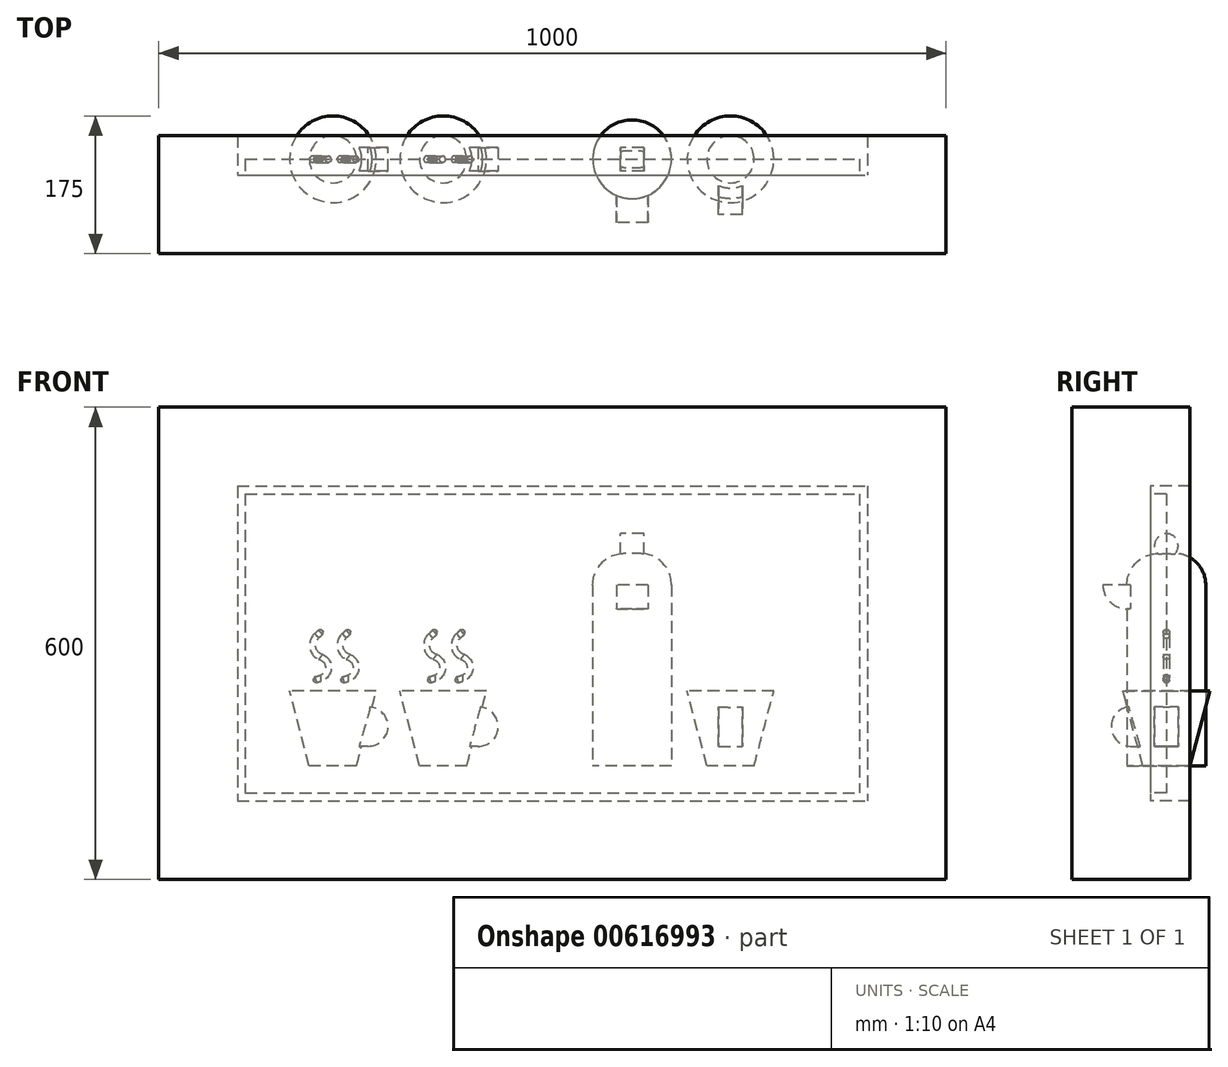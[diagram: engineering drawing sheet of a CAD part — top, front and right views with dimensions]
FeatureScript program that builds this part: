
annotation { "Feature Type Name" : "Feature", "Feature Type Description" : "" }
export const myFeature = defineFeature(function(context is Context, id is Id, definition is map)
    precondition{}
    {
        {
            var Q0;
            Q0=qCreatedBy(makeId("Top.planeOp"),FACE);
            cPlane(context, id + "F0", {"entities" : qUnion([Q0]), "cplaneType" : CPlaneType.OFFSET, "offset" : 95 * mm, "width" : 150 * mm, "height" : 150 * mm});
        }
        {
            var Q0;
            Q0=qCreatedBy(makeId("Top.planeOp"),FACE);
            var sketch = newSketch(context, id + "F1", { "sketchPlane" : qUnion([Q0])});
            skCircle(sketch, "E0", {"center": v(80, 0) * mm, "radius": 50 * mm});
            skSolve(sketch);
        }
        {
            var Q0;
            Q0=qSketchRegion(id+"F1",true);
            var Q1;
            Q1=qSketchRegion(id+"F3",true);
            extrude(context, id + "F2", {"entities" : qUnion([Q0, Q1]), "depth" : 230 * mm, "offsetDistance" : 25 * mm});
        }
        {
            var Q0;
            Q0=qCreatedBy(makeId("Top.planeOp"),FACE);
            var sketch = newSketch(context, id + "F3", { "sketchPlane" : qUnion([Q0])});
            skCircle(sketch, "E1", {"center": v(205, 0) * mm, "radius": 30 * mm});
            skSolve(sketch);
        }
        {
            var Q0;
            Q0=qCreatedBy(id+"F0.planeOp",FACE);
            var sketch = newSketch(context, id + "F4", { "sketchPlane" : qUnion([Q0])});
            skCircle(sketch, "E2", {"center": v(205, 0) * mm, "radius": 55 * mm});
            skSolve(sketch);
        }
        {
            var Q0;
            Q0=qCreatedBy(makeId("Top.planeOp"),FACE);
            cPlane(context, id + "F5", {"entities" : qUnion([Q0]), "cplaneType" : CPlaneType.OFFSET, "offset" : 230 * mm, "width" : 150 * mm, "height" : 150 * mm});
        }
        {
            var Q0;
            Q0=qCreatedBy(id+"F5.planeOp",FACE);
            var sketch = newSketch(context, id + "F6", { "sketchPlane" : qUnion([Q0])});
            skCircle(sketch, "E3", {"center": v(80, 0) * mm, "radius": 50 * mm});
            skSolve(sketch);
        }
        {
            var Q0;
            Q0 = qSketchRegion(id + "F6", true);
            extrude(context, id + "F7", {"entities" : qUnion([Q0]), "operationType" : NewBodyOperationType.ADD, "depth" : 40 * mm, "offsetDistance" : 25 * mm});
        }
        {
            var Q0;
            Q0=makeQuery(id+"F7.opExtrude","CAP_EDGE",EDGE,{"disambiguationData":[OSD([sQuery(id+"F6.wireOp",EDGE,"E3")])],"isStart":false});
            fillet(context, id + "F8", {"entities" : qUnion([Q0]), "radius" : 40 * mm, "tangentPropagation" : true, "allowEdgeOverflow" : false});
        }
        {
            var Q0;
            Q0=qSketchRegion(id+"F3",true);
            var Q1;
            Q1=qSketchRegion(id+"F4",true);
            loft(context, id + "F9", {"sheetProfilesArray" : [{ "sheetProfileEntities" : qUnion([Q0]) }, { "sheetProfileEntities" : qUnion([Q1]) }]});
        }
        {
            var Q0;
            Q0=qCreatedBy(makeId("Top.planeOp"),FACE);
            var sketch = newSketch(context, id + "F10", { "sketchPlane" : qUnion([Q0])});
            skCircle(sketch, "E4", {"center": v(-160, 0) * mm, "radius": 30 * mm});
            skSolve(sketch);
        }
        {
            var Q0;
            Q0=qCreatedBy(id+"F0.planeOp",FACE);
            var sketch = newSketch(context, id + "F11", { "sketchPlane" : qUnion([Q0])});
            skCircle(sketch, "E5", {"center": v(-160, 0) * mm, "radius": 55 * mm});
            skSolve(sketch);
        }
        {
            var Q0;
            Q0=qSketchRegion(id+"F10",true);
            var Q1;
            Q1=qSketchRegion(id+"F11",true);
            loft(context, id + "F12", {"sheetProfilesArray" : [{ "sheetProfileEntities" : qUnion([Q0]) }, { "sheetProfileEntities" : qUnion([Q1]) }]});
        }
        {
            var Q0;
            Q0=qCreatedBy(makeId("Top.planeOp"),FACE);
            var sketch = newSketch(context, id + "F13", { "sketchPlane" : qUnion([Q0])});
            skCircle(sketch, "E6", {"center": v(-300, 0) * mm, "radius": 30 * mm});
            skSolve(sketch);
        }
        {
            var Q0;
            Q0=qCreatedBy(id+"F0.planeOp",FACE);
            var sketch = newSketch(context, id + "F14", { "sketchPlane" : qUnion([Q0])});
            skCircle(sketch, "E7", {"center": v(-300, 0) * mm, "radius": 55 * mm});
            skSolve(sketch);
        }
        {
            var Q0;
            Q0=qSketchRegion(id+"F13",true);
            var Q1;
            Q1=qSketchRegion(id+"F14",true);
            loft(context, id + "F15", {"sheetProfilesArray" : [{ "sheetProfileEntities" : qUnion([Q0]) }, { "sheetProfileEntities" : qUnion([Q1]) }]});
        }
        {
            var Q0;
            Q0=qCreatedBy(makeId("Right.planeOp"),FACE);
            cPlane(context, id + "F16", {"entities" : qUnion([Q0]), "cplaneType" : CPlaneType.OFFSET, "offset" : 80 * mm, "width" : 150 * mm, "height" : 150 * mm});
        }
        {
            var Q0;
            Q0=qCreatedBy(id+"F16.planeOp",FACE);
            var sketch = newSketch(context, id + "F17", { "sketchPlane" : qUnion([Q0])});
            skCircle(sketch, "E8", {"center": v(0, 280) * mm, "radius": 15 * mm});
            skSolve(sketch);
        }
        {
            var Q0;
            Q0 = qSketchRegion(id + "F17", true);
            extrude(context, id + "F18", {"entities" : qUnion([Q0]), "operationType" : NewBodyOperationType.ADD, "endBound" : BoundingType.SYMMETRIC, "depth" : 30 * mm, "offsetDistance" : 25 * mm});
        }
        {
            var Q0;
            Q0=qCreatedBy(id+"F16.planeOp",FACE);
            var sketch = newSketch(context, id + "F19", { "sketchPlane" : qUnion([Q0])});
            skArc(sketch, "E9", {"start": v(-80.58, 229.93) * mm, "mid": v(-50, 199.42) * mm, "end": v(-19.42, 229.93) * mm});
            skLineSegment(sketch, "E10", {"start": v(-19.42, 229.93) * mm, "end": v(-80.58, 229.93) * mm});
            skSolve(sketch);
        }
        {
            var Q0;
            Q0=qSketchRegion(id+"F19",true);
            extrude(context, id + "F20", {"entities" : qUnion([Q0]), "operationType" : NewBodyOperationType.ADD, "endBound" : BoundingType.SYMMETRIC, "depth" : 40 * mm, "offsetDistance" : 25 * mm});
        }
        {
            var Q0;
            Q0=qCreatedBy(makeId("Right.planeOp"),FACE);
            cPlane(context, id + "F21", {"entities" : qUnion([Q0]), "cplaneType" : CPlaneType.OFFSET, "offset" : 205 * mm, "width" : 150 * mm, "height" : 150 * mm});
        }
        {
            var Q0;
            Q0=qCreatedBy(id+"F21.planeOp",FACE);
            var sketch = newSketch(context, id + "F22", { "sketchPlane" : qUnion([Q0])});
            skArc(sketch, "E11", {"start": v(-44.02, 74.98) * mm, "mid": v(-69.99, 50.74) * mm, "end": v(-45.51, 25) * mm});
            skLineSegment(sketch, "E12", {"start": v(-45.51, 25) * mm, "end": v(-13.64, 24.35) * mm});
            skLineSegment(sketch, "E13", {"start": v(-13.64, 24.35) * mm, "end": v(-13.64, 73.8) * mm});
            skLineSegment(sketch, "E14", {"start": v(-13.64, 73.8) * mm, "end": v(-44.02, 74.98) * mm});
            skSolve(sketch);
        }
        {
            var Q0;
            Q0=qSketchRegion(id+"F22",true);
            extrude(context, id + "F23", {"entities" : qUnion([Q0]), "operationType" : NewBodyOperationType.ADD, "endBound" : BoundingType.SYMMETRIC, "depth" : 30 * mm, "offsetDistance" : 25 * mm});
        }
        {
            var Q0;
            Q0=qCreatedBy(makeId("Front.planeOp"),FACE);
            var sketch = newSketch(context, id + "F24", { "sketchPlane" : qUnion([Q0])});
            skArc(sketch, "E15", {"start": v(-115.89, 25.02) * mm, "mid": v(-90, 49.5) * mm, "end": v(-114.88, 75) * mm});
            skLineSegment(sketch, "E16", {"start": v(-115.89, 25.02) * mm, "end": v(-153.4, 25.02) * mm});
            skLineSegment(sketch, "E17", {"start": v(-153.4, 25.02) * mm, "end": v(-153.4, 75.18) * mm});
            skLineSegment(sketch, "E18", {"start": v(-153.4, 75.18) * mm, "end": v(-114.88, 75) * mm});
            skSolve(sketch);
        }
        {
            var Q0;
            Q0=qSketchRegion(id+"F24",true);
            extrude(context, id + "F25", {"entities" : qUnion([Q0]), "operationType" : NewBodyOperationType.ADD, "endBound" : BoundingType.SYMMETRIC, "oppositeDirection" : true, "depth" : 30 * mm, "offsetDistance" : 25 * mm});
        }
        {
            var Q0;
            Q0=qCreatedBy(makeId("Front.planeOp"),FACE);
            var sketch = newSketch(context, id + "F26", { "sketchPlane" : qUnion([Q0])});
            skArc(sketch, "E19", {"start": v(-255.26, 25) * mm, "mid": v(-230, 50.18) * mm, "end": v(-255.62, 75) * mm});
            skLineSegment(sketch, "E20", {"start": v(-254.74, 25) * mm, "end": v(-297.4, 25) * mm});
            skLineSegment(sketch, "E21", {"start": v(-297.4, 25) * mm, "end": v(-297.4, 73.96) * mm});
            skLineSegment(sketch, "E22", {"start": v(-297.4, 73.96) * mm, "end": v(-255.62, 75) * mm});
            skSolve(sketch);
        }
        {
            var Q0;
            Q0=qSketchRegion(id+"F26",true);
            extrude(context, id + "F27", {"entities" : qUnion([Q0]), "operationType" : NewBodyOperationType.ADD, "endBound" : BoundingType.SYMMETRIC, "depth" : 30 * mm, "offsetDistance" : 25 * mm});
        }
        {
            var Q0;
            Q0=qCreatedBy(makeId("Right.planeOp"),FACE);
            cPlane(context, id + "F28", {"entities" : qUnion([Q0]), "cplaneType" : CPlaneType.OFFSET, "offset" : 140 * mm, "oppositeDirection" : true, "width" : 150 * mm, "height" : 150 * mm});
        }
        {
            var Q0;
            Q0=qCreatedBy(makeId("Front.planeOp"),FACE);
            var sketch = newSketch(context, id + "F29", { "sketchPlane" : qUnion([Q0])});
            skArc(sketch, "E23", {"start": v(-140, 164.46) * mm, "mid": v(-144.72, 150.38) * mm, "end": v(-135, 139.14) * mm});
            skArc(sketch, "E24", {"start": v(-135, 110.86) * mm, "mid": v(-125, 125) * mm, "end": v(-135, 139.14) * mm});
            skPoint(sketch, "E25", {"position": v(-135, 110.86) * mm});
            skPoint(sketch, "E26", {"position": v(-135, 139.14) * mm});
            skPoint(sketch, "E27", {"position": v(-140, 164.46) * mm});
            skLineSegment(sketch, "E28", {"start": v(-135, 110.86) * mm, "end": v(-144.43, 107.52) * mm});
            skFitSpline(sketch, "E29", {"points": [v(-140, 164.46) * mm, v(-133.14, 171.17) * mm], "startDerivative": vector(6.86, 6.7) * mm, "endDerivative": vector(6.86, 6.7) * mm});
            skSolve(sketch);
        }
        {
            var Q0;
            Q0=qCreatedBy(id+"F28.planeOp",FACE);
            var sketch = newSketch(context, id + "F30", { "sketchPlane" : qUnion([Q0])});
            skCircle(sketch, "E30", {"center": v(0, 110) * mm, "radius": 4 * mm});
            skSolve(sketch);
        }
        {
            var Q0;
            Q0=makeQuery(id+"F30.imprint","IMPRINT",FACE,{"disambiguationData":[TD([[makeQuery(id+"F30.imprint","IMPRINT",EDGE,{"derivedFrom":sQuery(id+"F30.wireOp",EDGE,"E30")}),1.0]])]});
            var Q1;
            Q1=sQuery(id+"F29.wireOp",EDGE,"E29");
            var Q2;
            Q2=sQuery(id+"F29.wireOp",EDGE,"E23");
            var Q3;
            Q3=sQuery(id+"F29.wireOp",EDGE,"E24");
            var Q4;
            Q4=sQuery(id+"F29.wireOp",EDGE,"E28");
            sweep(context, id + "F31", {"profiles" : qUnion([Q0]), "path" : qUnion([Q1, Q2, Q3, Q4])});
        }
        {
            var Q0;
            Q0=makeQuery(id+"F31.opSweep","CAP_EDGE",EDGE,{"disambiguationData":[OSD([sQuery(id+"F29.wireOp",VERTEX,"E28.end"),sQuery(id+"F30.wireOp",EDGE,"E30")])],"isStart":true});
            fillet(context, id + "F32", {"entities" : qUnion([Q0]), "radius" : 3 * mm, "allowEdgeOverflow" : false});
        }
        {
            var Q0;
            Q0=makeQuery(id+"F31.opSweep","CAP_EDGE",EDGE,{"disambiguationData":[OSD([sQuery(id+"F29.wireOp",VERTEX,"E29.end"),sQuery(id+"F30.wireOp",EDGE,"E30")])],"isStart":false});
            fillet(context, id + "F33", {"entities" : qUnion([Q0]), "radius" : 3 * mm, "tangentPropagation" : true, "allowEdgeOverflow" : false});
        }
        {
            var Q0;
            Q0=qCreatedBy(makeId("Front.planeOp"),FACE);
            cPlane(context, id + "F34", {"entities" : qUnion([Q0]), "cplaneType" : CPlaneType.OFFSET, "offset" : 20 * mm, "width" : 150 * mm, "height" : 150 * mm});
        }
        {
            var Q0;
            Q0=qCreatedBy(id+"F34.planeOp",FACE);
            var sketch = newSketch(context, id + "F35", { "sketchPlane" : qUnion([Q0])});
            skLineSegment(sketch, "E31.bottom", {"start": v(-421.33, 355.64) * mm, "end": v(378.67, 355.64) * mm});
            skLineSegment(sketch, "E31.top", {"start": v(-421.33, -44.36) * mm, "end": v(378.67, -44.36) * mm});
            skLineSegment(sketch, "E31.left", {"start": v(-421.33, 355.64) * mm, "end": v(-421.33, -44.36) * mm});
            skLineSegment(sketch, "E31.right", {"start": v(378.67, 355.64) * mm, "end": v(378.67, -44.36) * mm});
            skSolve(sketch);
        }
        {
            var Q0;
            Q0=qCreatedBy(makeId("Front.planeOp"),FACE);
            cPlane(context, id + "F36", {"entities" : qUnion([Q0]), "cplaneType" : CPlaneType.OFFSET, "offset" : 30 * mm, "oppositeDirection" : true, "width" : 150 * mm, "height" : 150 * mm});
        }
        {
            var Q0;
            Q0=qSketchRegion(id+"F35",true);
            extrude(context, id + "F37", {"entities" : qUnion([Q0]), "oppositeDirection" : true, "depth" : 60 * mm, "offsetDistance" : 25 * mm});
        }
        {
            var Q0;
            Q0=qCreatedBy(id+"F34.planeOp",FACE);
            var sketch = newSketch(context, id + "F38", { "sketchPlane" : qUnion([Q0])});
            skLineSegment(sketch, "E32.bottom", {"start": v(-411.33, 345.64) * mm, "end": v(368.67, 345.64) * mm});
            skLineSegment(sketch, "E32.top", {"start": v(-411.33, -34.36) * mm, "end": v(368.67, -34.36) * mm});
            skLineSegment(sketch, "E32.left", {"start": v(-411.33, 345.64) * mm, "end": v(-411.33, -34.36) * mm});
            skLineSegment(sketch, "E32.right", {"start": v(368.67, 345.64) * mm, "end": v(368.67, -34.36) * mm});
            skSolve(sketch);
        }
        {
            var Q0;
            Q0=qSketchRegion(id+"F38",true);
            extrude(context, id + "F39", {"entities" : qUnion([Q0]), "oppositeDirection" : true, "depth" : 20 * mm, "offsetDistance" : 25 * mm});
        }
        {
            var Q0;
            Q0=qCreatedBy(id+"F36.planeOp",FACE);
            var sketch = newSketch(context, id + "F40", { "sketchPlane" : qUnion([Q0])});
            skLineSegment(sketch, "E33.bottom", {"start": v(-521.33, 455.64) * mm, "end": v(478.67, 455.64) * mm});
            skLineSegment(sketch, "E33.top", {"start": v(-521.33, -144.36) * mm, "end": v(478.67, -144.36) * mm});
            skLineSegment(sketch, "E33.left", {"start": v(-521.33, 455.64) * mm, "end": v(-521.33, -144.36) * mm});
            skLineSegment(sketch, "E33.right", {"start": v(478.67, 455.64) * mm, "end": v(478.67, -144.36) * mm});
            skSolve(sketch);
        }
        {
            var Q0;
            Q0=qSketchRegion(id+"F40",true);
            extrude(context, id + "F41", {"entities" : qUnion([Q0]), "depth" : 150 * mm, "offsetDistance" : 25 * mm});
        }
        {
            var Q0;
            Q0=makeQuery(id+"F39.opExtrude","SWEPT_BODY",BODY,{"disambiguationData":[OSD([sQuery(id+"F38.wireOp",EDGE,"E32.bottom"),sQuery(id+"F38.wireOp",EDGE,"E32.top"),sQuery(id+"F38.wireOp",EDGE,"E32.left"),sQuery(id+"F38.wireOp",EDGE,"E32.right")])]});
            var Q1;
            Q1=makeQuery(id+"F37.opExtrude","SWEPT_BODY",BODY,{"disambiguationData":[OSD([sQuery(id+"F35.wireOp",EDGE,"E31.bottom"),sQuery(id+"F35.wireOp",EDGE,"E31.top"),sQuery(id+"F35.wireOp",EDGE,"E31.left"),sQuery(id+"F35.wireOp",EDGE,"E31.right")])]});
            booleanBodies(context, id + "F42", {"operationType" : BooleanOperationType.SUBTRACTION, "tools" : qUnion([Q0]), "targets" : qUnion([Q1])});
        }
        {
            var Q0;
            Q0=makeQuery(id+"F37.opExtrude","SWEPT_BODY",BODY,{"disambiguationData":[OSD([sQuery(id+"F35.wireOp",EDGE,"E31.bottom"),sQuery(id+"F35.wireOp",EDGE,"E31.top"),sQuery(id+"F35.wireOp",EDGE,"E31.left"),sQuery(id+"F35.wireOp",EDGE,"E31.right")])]});
            var Q1;
            Q1=makeQuery(id+"F41.opExtrude","SWEPT_BODY",BODY,{"disambiguationData":[OSD([sQuery(id+"F40.wireOp",EDGE,"E33.bottom"),sQuery(id+"F40.wireOp",EDGE,"E33.top"),sQuery(id+"F40.wireOp",EDGE,"E33.left"),sQuery(id+"F40.wireOp",EDGE,"E33.right")])]});
            booleanBodies(context, id + "F43", {"operationType" : BooleanOperationType.SUBTRACTION, "tools" : qUnion([Q0]), "targets" : qUnion([Q1])});
        }
        {
            var Q0;
            Q0=makeQuery(id+"F31.opSweep","SWEPT_BODY",BODY,{"disambiguationData":[OSD([sQuery(id+"F29.wireOp",EDGE,"E28"),sQuery(id+"F30.wireOp",EDGE,"E30")])]});
            transform(context, id + "F44", {"entities" : qUnion([Q0]), "transformType" : TransformType.TRANSLATION_3D, "dx" : -35 * mm, "dy" : 0 * mm, "dz" : 0 * mm, "makeCopy" : true});
        }
        {
            var Q0;
            Q0=makeQuery(id+"F44.opPattern","COPY",BODY,{"derivedFrom":makeQuery(id+"F31.opSweep","SWEPT_BODY",BODY,{"disambiguationData":[OSD([sQuery(id+"F29.wireOp",EDGE,"E28"),sQuery(id+"F30.wireOp",EDGE,"E30")])]}),"instanceName":"1"});
            transform(context, id + "F45", {"entities" : qUnion([Q0]), "transformType" : TransformType.TRANSLATION_3D, "dx" : -105 * mm, "dy" : 0 * mm, "dz" : 0 * mm, "makeCopy" : true});
        }
        {
            var Q0;
            Q0=makeQuery(id+"F45.opPattern","COPY",BODY,{"derivedFrom":makeQuery(id+"F44.opPattern","COPY",BODY,{"derivedFrom":makeQuery(id+"F31.opSweep","SWEPT_BODY",BODY,{"disambiguationData":[OSD([sQuery(id+"F29.wireOp",EDGE,"E28"),sQuery(id+"F30.wireOp",EDGE,"E30")])]}),"instanceName":"1"}),"instanceName":"1"});
            transform(context, id + "F46", {"entities" : qUnion([Q0]), "transformType" : TransformType.TRANSLATION_3D, "dx" : -35 * mm, "dy" : 0 * mm, "dz" : 0 * mm, "makeCopy" : true});
        }
        {
            var Q0;
            Q0=makeQuery(id+"F44.opPattern","COPY",BODY,{"derivedFrom":makeQuery(id+"F31.opSweep","SWEPT_BODY",BODY,{"disambiguationData":[OSD([sQuery(id+"F29.wireOp",EDGE,"E28"),sQuery(id+"F30.wireOp",EDGE,"E30")])]}),"instanceName":"1"});
            var Q1;
            Q1=makeQuery(id+"F45.opPattern","COPY",BODY,{"derivedFrom":makeQuery(id+"F44.opPattern","COPY",BODY,{"derivedFrom":makeQuery(id+"F31.opSweep","SWEPT_BODY",BODY,{"disambiguationData":[OSD([sQuery(id+"F29.wireOp",EDGE,"E28"),sQuery(id+"F30.wireOp",EDGE,"E30")])]}),"instanceName":"1"}),"instanceName":"1"});
            var Q2;
            Q2=makeQuery(id+"F46.opPattern","COPY",BODY,{"derivedFrom":makeQuery(id+"F45.opPattern","COPY",BODY,{"derivedFrom":makeQuery(id+"F44.opPattern","COPY",BODY,{"derivedFrom":makeQuery(id+"F31.opSweep","SWEPT_BODY",BODY,{"disambiguationData":[OSD([sQuery(id+"F29.wireOp",EDGE,"E28"),sQuery(id+"F30.wireOp",EDGE,"E30")])]}),"instanceName":"1"}),"instanceName":"1"}),"instanceName":"1"});
            deleteBodies(context, id + "F47", {"entities" : qUnion([Q0, Q1, Q2])});
        }
        {
            var Q0;
            Q0=makeQuery(id+"F31.opSweep","SWEPT_BODY",BODY,{"disambiguationData":[OSD([sQuery(id+"F29.wireOp",EDGE,"E28"),sQuery(id+"F30.wireOp",EDGE,"E30")])]});
            transform(context, id + "F48", {"entities" : qUnion([Q0]), "transformType" : TransformType.TRANSLATION_3D, "dx" : -35 * mm, "dy" : 0 * mm, "dz" : 0 * mm, "makeCopy" : true});
        }
        {
            var Q0;
            Q0=makeQuery(id+"F48.opPattern","COPY",BODY,{"derivedFrom":makeQuery(id+"F31.opSweep","SWEPT_BODY",BODY,{"disambiguationData":[OSD([sQuery(id+"F29.wireOp",EDGE,"E28"),sQuery(id+"F30.wireOp",EDGE,"E30")])]}),"instanceName":"1"});
            transform(context, id + "F49", {"entities" : qUnion([Q0]), "transformType" : TransformType.TRANSLATION_3D, "dx" : -110 * mm, "dy" : 0 * mm, "dz" : 0 * mm, "makeCopy" : true});
        }
        {
            var Q0;
            Q0=makeQuery(id+"F49.opPattern","COPY",BODY,{"derivedFrom":makeQuery(id+"F48.opPattern","COPY",BODY,{"derivedFrom":makeQuery(id+"F31.opSweep","SWEPT_BODY",BODY,{"disambiguationData":[OSD([sQuery(id+"F29.wireOp",EDGE,"E28"),sQuery(id+"F30.wireOp",EDGE,"E30")])]}),"instanceName":"1"}),"instanceName":"1"});
            transform(context, id + "F50", {"entities" : qUnion([Q0]), "transformType" : TransformType.TRANSLATION_3D, "dx" : -35 * mm, "dy" : 0 * mm, "dz" : 0 * mm, "makeCopy" : true});
        }
    });
